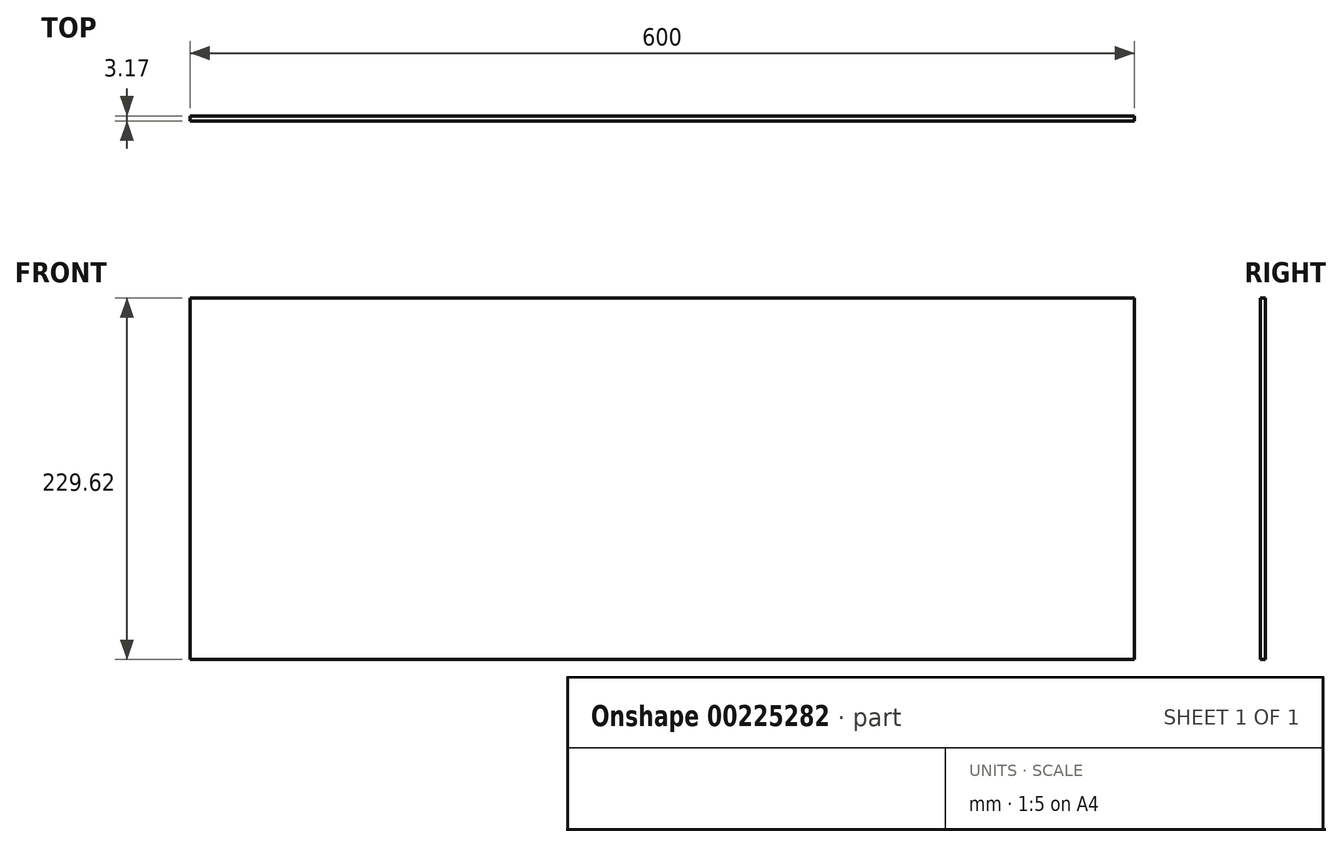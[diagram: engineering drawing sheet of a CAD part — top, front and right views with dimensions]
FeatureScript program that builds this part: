
annotation { "Feature Type Name" : "Feature", "Feature Type Description" : "" }
export const myFeature = defineFeature(function(context is Context, id is Id, definition is map)
    precondition{}
    {
        {
            var Q0;
            Q0=qCreatedBy(makeId("Front.planeOp"),FACE);
            var sketch = newSketch(context, id + "F0", { "sketchPlane" : qUnion([Q0])});
            skLineSegment(sketch, "E0.bottom", {"start": v(300, 114.8) * mm, "end": v(-300, 114.8) * mm});
            skLineSegment(sketch, "E0.top", {"start": v(300, -114.8) * mm, "end": v(-300, -114.8) * mm});
            skLineSegment(sketch, "E0.left", {"start": v(300, 114.8) * mm, "end": v(300, -114.8) * mm});
            skLineSegment(sketch, "E0.right", {"start": v(-300, 114.8) * mm, "end": v(-300, -114.8) * mm});
            skPoint(sketch, "E0.middle", {"position": v(0, 0) * mm});
            skSolve(sketch);
        }
        {
            var Q0;
            Q0=makeQuery(id+"F0.imprint","IMPRINT",FACE,{"disambiguationData":[TD([[makeQuery(id+"F0.imprint","IMPRINT",EDGE,{"derivedFrom":sQuery(id+"F0.wireOp",EDGE,"E0.bottom")}),1.0]])]});
            extrude(context, id + "F1", {"entities" : qUnion([Q0]), "depth" : 3.17 * mm});
        }
    });
